# Revit family: 57_CRD_ME_Minibox
name_source: partatom
category: Mechanical Equipment
units: mm (PartAtom-declared; Revit-internal decimal feet)

## family parameters
Always vertical = No
Classification = None
Cut with Voids When Loaded = No
OmniClass Number = 23.75.70.21.31
OmniClass Title = Exhaust Terminals
Part Type = Normal
Room Calculation Point = Yes
Round Connector Dimension = Use Radius
Shared = No
Work Plane-Based = Yes

## types (1)
- MiniBox
    Default Elevation = 1219 mm
    IFCExportAs = IfcAirTerminalBox
    IFCExportType = NOTDEFINED
    Manufacturer = ClimaRad
    Model = Minibox
    Power = 25 W
    Voltage = 230 V
    breedte = 192 mm
    hoogte = 215 mm  [stored 0.705381 ft]
    lengte = 280 mm
    materiaal = Color RAL 9003
    radius = 50 mm  [stored 0.164042 ft]

note: [stored X ft] marks values corroborated as IEEE doubles in the binary element streams (Revit-internal decimal feet)

## geometry (parser evidence)
native form markers: Sweep x10
no freeform markers — native parametric forms only
